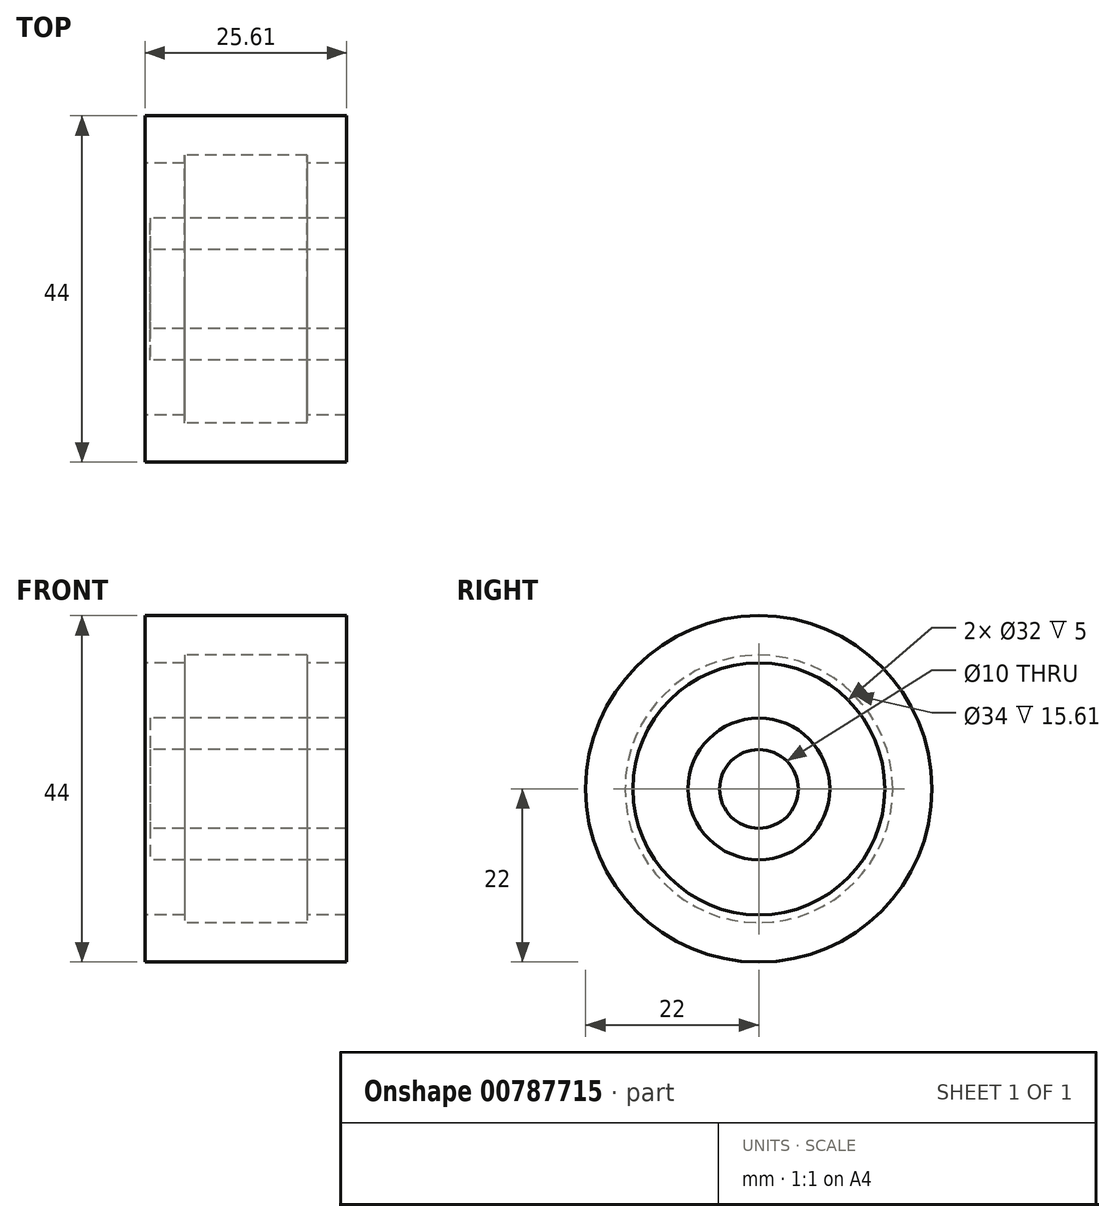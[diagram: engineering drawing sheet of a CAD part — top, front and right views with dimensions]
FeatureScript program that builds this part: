
annotation { "Feature Type Name" : "Feature", "Feature Type Description" : "" }
export const myFeature = defineFeature(function(context is Context, id is Id, definition is map)
    precondition{}
    {
        {
            var Q0;
            Q0=qCreatedBy(makeId("Front.planeOp"),FACE);
            var sketch = newSketch(context, id + "F0", { "sketchPlane" : qUnion([Q0])});
            skLineSegment(sketch, "E0", {"start": v(-44.87, 0) * mm, "end": v(44.13, 0) * mm});
            skLineSegment(sketch, "E1.bottom", {"start": v(-13, 5) * mm, "end": v(12, 5) * mm});
            skLineSegment(sketch, "E1.left", {"start": v(-13, 5) * mm, "end": v(-13, 9) * mm});
            skLineSegment(sketch, "E1.right", {"start": v(12, 5) * mm, "end": v(12, 9) * mm});
            skLineSegment(sketch, "E2", {"start": v(-13.6, 16) * mm, "end": v(-8.6, 16) * mm});
            skLineSegment(sketch, "E3", {"start": v(-8.6, 16) * mm, "end": v(-8.6, 17) * mm});
            skLineSegment(sketch, "E4", {"start": v(-8.6, 17) * mm, "end": v(7, 17) * mm});
            skLineSegment(sketch, "E5", {"start": v(7, 17) * mm, "end": v(7, 16) * mm});
            skLineSegment(sketch, "E6", {"start": v(7, 16) * mm, "end": v(12, 16) * mm});
            skLineSegment(sketch, "E7", {"start": v(12, 16) * mm, "end": v(12, 22) * mm});
            skLineSegment(sketch, "E8", {"start": v(12, 22) * mm, "end": v(-13.6, 22) * mm});
            skLineSegment(sketch, "E9", {"start": v(-13.6, 22) * mm, "end": v(-13.6, 16) * mm});
            skLineSegment(sketch, "E10", {"start": v(-13, 9) * mm, "end": v(12, 9) * mm});
            skSolve(sketch);
        }
        {
            var Q0;
            Q0 = qSketchRegion(id + "F0", true);
            var Q1;
            Q1=sQuery(id+"F0.wireOp",EDGE,"E0");
            revolve(context, id + "F1", {"surfaceOperationType" : NewSurfaceOperationType.NEW, "entities" : qUnion([Q0]), "axis" : qUnion([Q1]), "revolveType" : RevolveType.FULL});
        }
    });
